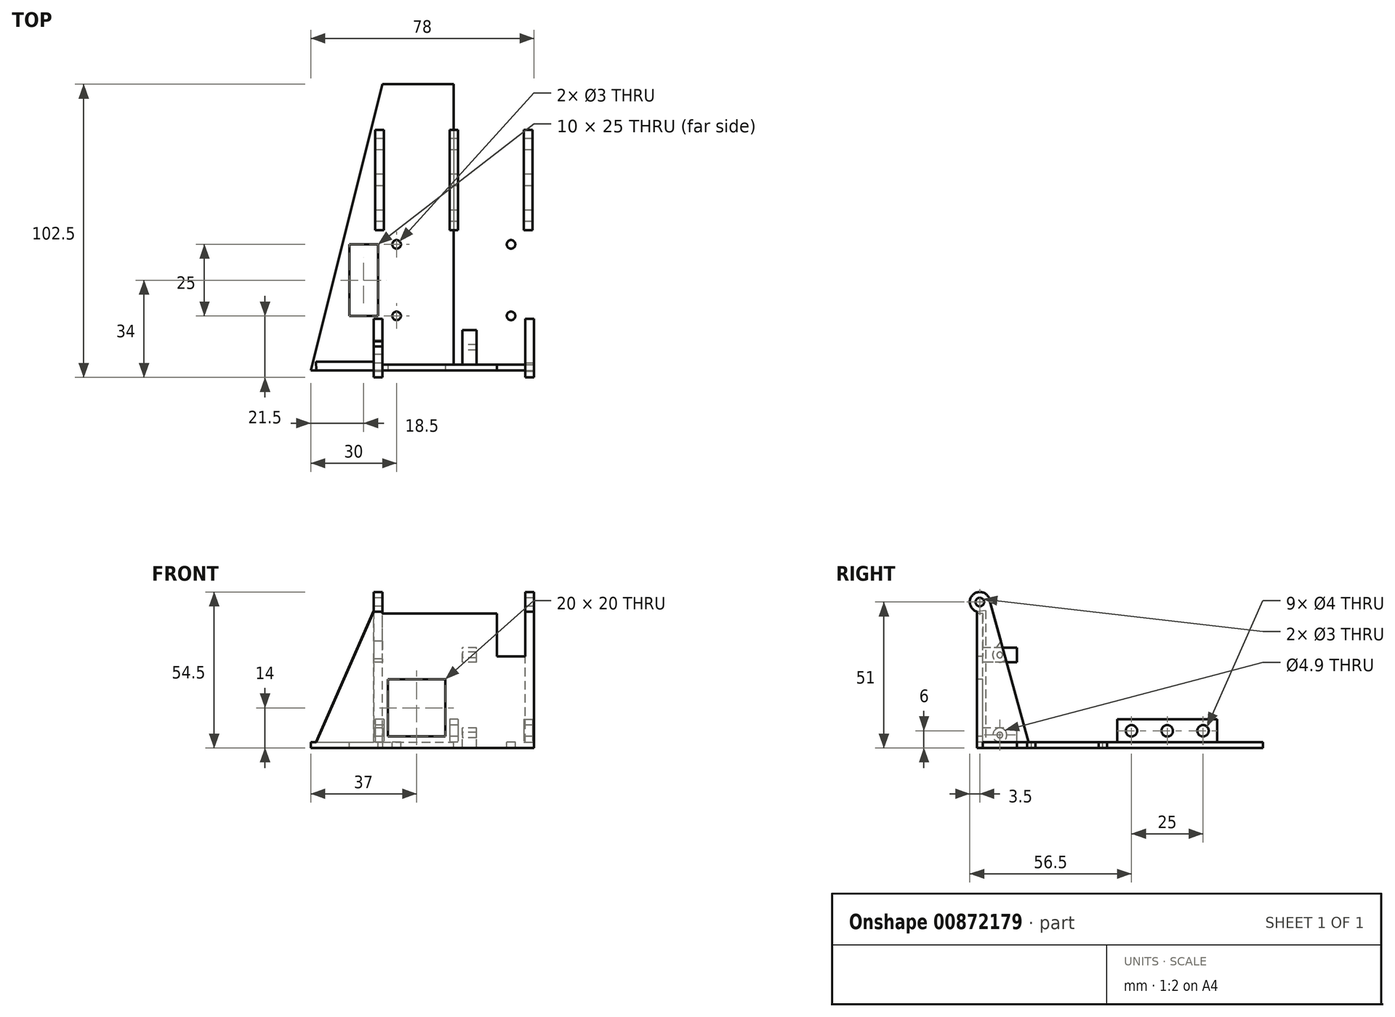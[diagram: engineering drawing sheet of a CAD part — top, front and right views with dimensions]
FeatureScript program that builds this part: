
annotation { "Feature Type Name" : "Feature", "Feature Type Description" : "" }
export const myFeature = defineFeature(function(context is Context, id is Id, definition is map)
    precondition{}
    {
        {
            var Q0;
            Q0=qCreatedBy(makeId("Top.planeOp"),FACE);
            var sketch = newSketch(context, id + "F0", { "sketchPlane" : qUnion([Q0])});
            skLineSegment(sketch, "E0.bottom", {"start": v(25, -50) * mm, "end": v(-25, -50) * mm});
            skLineSegment(sketch, "E0.top", {"start": v(25, 50) * mm, "end": v(-25, 50) * mm});
            skLineSegment(sketch, "E0.left", {"start": v(25, -50) * mm, "end": v(25, 50) * mm});
            skLineSegment(sketch, "E0.right", {"start": v(-25, -50) * mm, "end": v(-25, 50) * mm});
            skPoint(sketch, "E0.middle", {"position": v(0, 0) * mm});
            skLineSegment(sketch, "E1", {"start": v(-25, -50) * mm, "end": v(-50, -50) * mm});
            skLineSegment(sketch, "E2", {"start": v(-50, -50) * mm, "end": v(-25, 50) * mm});
            skLineSegment(sketch, "E3", {"start": v(25, -50) * mm, "end": v(50, -50) * mm});
            skLineSegment(sketch, "E4", {"start": v(50, -50) * mm, "end": v(25, 50) * mm});
            skSolve(sketch);
        }
        {
            var Q0;
            Q0=makeQuery(id+"F0.imprint","IMPRINT",FACE,{"disambiguationData":[TD([[makeQuery(id+"F0.imprint","IMPRINT",EDGE,{"derivedFrom":sQuery(id+"F0.wireOp",EDGE,"E0.left")}),-1.0]])]});
            var Q1;
            Q1=makeQuery(id+"F0.imprint","IMPRINT",FACE,{"disambiguationData":[TD([[makeQuery(id+"F0.imprint","IMPRINT",EDGE,{"derivedFrom":sQuery(id+"F0.wireOp",EDGE,"E0.right")}),1.0]])]});
            var Q2;
            Q2=makeQuery(id+"F0.imprint","IMPRINT",FACE,{"disambiguationData":[TD([[makeQuery(id+"F0.imprint","IMPRINT",EDGE,{"derivedFrom":sQuery(id+"F0.wireOp",EDGE,"E0.bottom")}),-1.0]])]});
            extrude(context, id + "F1", {"entities" : qUnion([Q0, Q1, Q2]), "depth" : 2 * mm, "offsetDistance" : 25 * mm});
        }
        {
            var Q0;
            Q0=qCreatedBy(makeId("Right.planeOp"),FACE);
            var sketch = newSketch(context, id + "F2", { "sketchPlane" : qUnion([Q0])});
            skLineSegment(sketch, "E5.bottom", {"start": v(-50, 0) * mm, "end": v(-48, 0) * mm});
            skLineSegment(sketch, "E5.top", {"start": v(-50, 47) * mm, "end": v(-48, 47) * mm});
            skLineSegment(sketch, "E5.left", {"start": v(-50, 0) * mm, "end": v(-50, 47) * mm});
            skLineSegment(sketch, "E5.right", {"start": v(-48, 0) * mm, "end": v(-48, 47) * mm});
            skSolve(sketch);
        }
        {
            var Q0;
            Q0=makeQuery(id+"F2.imprint","IMPRINT",FACE,{"disambiguationData":[TD([[makeQuery(id+"F2.imprint","IMPRINT",EDGE,{"derivedFrom":sQuery(id+"F2.wireOp",EDGE,"E5.bottom")}),1.0]])]});
            extrude(context, id + "F3", {"entities" : qUnion([Q0]), "operationType" : NewBodyOperationType.ADD, "endBound" : BoundingType.SYMMETRIC, "depth" : 56 * mm, "offsetDistance" : 25 * mm});
        }
        {
            var Q0;
            Q0=makeQuery(id+"F3.opExtrude","CAP_FACE",FACE,{"disambiguationData":[OSD([sQuery(id+"F2.wireOp",EDGE,"E5.bottom"),sQuery(id+"F2.wireOp",EDGE,"E5.top"),sQuery(id+"F2.wireOp",EDGE,"E5.left"),sQuery(id+"F2.wireOp",EDGE,"E5.right")])],"isStart":false});
            var sketch = newSketch(context, id + "F4", { "sketchPlane" : qUnion([Q0])});
            skPoint(sketch, "E6.centerSnap0", {"position": v(-49, 47) * mm});
            skCircle(sketch, "E7", {"center": v(-49, 51) * mm, "radius": 3.5 * mm});
            skLineSegment(sketch, "E8", {"start": v(-48, 47) * mm, "end": v(-48, 47.65) * mm});
            skLineSegment(sketch, "E9", {"start": v(-50, 47) * mm, "end": v(-50, 47.65) * mm});
            skSolve(sketch);
        }
        {
            var Q0;
            {var subQ5=makeQuery(id+"F3.opExtrude","CAP_EDGE",EDGE,{"disambiguationData":[OSD([sQuery(id+"F2.wireOp",EDGE,"E5.top")])],"isStart":false});Q0=makeQuery(id+"F4.imprint","IMPRINT",FACE,{"disambiguationData":[TD([[makeQuery(id+"F4.imprint","IMPRINT",EDGE,{"derivedFrom":subQ5}),1.0]])]});}
            var Q1;
            {var subQ0=sQuery(id+"F4.wireOp",EDGE,"E7");var subQ1=makeQuery(id+"F4.imprint","INTERSECT",VERTEX,{"derivedFrom":[subQ0,sQuery(id+"F4.wireOp",EDGE,"E8")]});Q1=makeQuery(id+"F4.imprint","IMPRINT",FACE,{"disambiguationData":[TD([[makeQuery(id+"F4.imprint","IMPRINT",EDGE,{"disambiguationData":[TD([[subQ1,1.0]])],"derivedFrom":subQ0}),1.0]])]});}
            extrude(context, id + "F5", {"entities" : qUnion([Q0, Q1]), "operationType" : NewBodyOperationType.ADD, "oppositeDirection" : true, "depth" : 3 * mm, "offsetDistance" : 25 * mm});
        }
        {
            var Q0;
            Q0=makeQuery(id+"F3.opExtrude","CAP_FACE",FACE,{"disambiguationData":[OSD([sQuery(id+"F2.wireOp",EDGE,"E5.bottom"),sQuery(id+"F2.wireOp",EDGE,"E5.top"),sQuery(id+"F2.wireOp",EDGE,"E5.left"),sQuery(id+"F2.wireOp",EDGE,"E5.right")])],"isStart":true});
            var sketch = newSketch(context, id + "F6", { "sketchPlane" : qUnion([Q0])});
            skCircle(sketch, "E10", {"center": v(49, 51) * mm, "radius": 3.5 * mm});
            skPoint(sketch, "E10.centerSnap0", {"position": v(49, 47) * mm});
            skLineSegment(sketch, "E11", {"start": v(48, 47) * mm, "end": v(48, 47.65) * mm});
            skLineSegment(sketch, "E12", {"start": v(50, 47) * mm, "end": v(50, 47.65) * mm});
            skSolve(sketch);
        }
        {
            var Q0;
            {var subQ5=makeQuery(id+"F3.opExtrude","CAP_EDGE",EDGE,{"disambiguationData":[OSD([sQuery(id+"F2.wireOp",EDGE,"E5.top")])],"isStart":true});Q0=makeQuery(id+"F6.imprint","IMPRINT",FACE,{"disambiguationData":[TD([[makeQuery(id+"F6.imprint","IMPRINT",EDGE,{"derivedFrom":subQ5}),-1.0]])]});}
            var Q1;
            {var subQ0=sQuery(id+"F6.wireOp",EDGE,"E10");var subQ1=makeQuery(id+"F6.imprint","INTERSECT",VERTEX,{"derivedFrom":[subQ0,sQuery(id+"F6.wireOp",EDGE,"E11")]});Q1=makeQuery(id+"F6.imprint","IMPRINT",FACE,{"disambiguationData":[TD([[makeQuery(id+"F6.imprint","IMPRINT",EDGE,{"disambiguationData":[TD([[subQ1,-1.0]])],"derivedFrom":subQ0}),1.0]])]});}
            extrude(context, id + "F7", {"entities" : qUnion([Q0, Q1]), "operationType" : NewBodyOperationType.ADD, "oppositeDirection" : true, "depth" : 3 * mm, "offsetDistance" : 25 * mm});
        }
        {
            var Q0;
            {var subQ0=sQuery(id+"F2.wireOp",EDGE,"E5.right");var subQ1=sQuery(id+"F2.wireOp",EDGE,"E5.left");var subQ2=sQuery(id+"F2.wireOp",EDGE,"E5.top");Q0=makeQuery(id+"F7.boolean.opBoolean","MERGE",FACE,{"derivedFrom":[makeQuery(id+"F3.opExtrude","CAP_FACE",FACE,{"disambiguationData":[OSD([sQuery(id+"F2.wireOp",EDGE,"E5.bottom"),subQ2,subQ1,subQ0])],"isStart":true}),makeQuery(id+"F7.opExtrude","CAP_FACE",FACE,{"disambiguationData":[OSD([subQ2,subQ1,subQ0,sQuery(id+"F6.wireOp",EDGE,"E10")])],"isStart":true})]});}
            var sketch = newSketch(context, id + "F8", { "sketchPlane" : qUnion([Q0])});
            skCircle(sketch, "E13", {"center": v(49, 51) * mm, "radius": 1.5 * mm});
            skSolve(sketch);
        }
        {
            var Q0;
            Q0=makeQuery(id+"F8.imprint","IMPRINT",FACE,{"disambiguationData":[TD([[makeQuery(id+"F8.imprint","IMPRINT",EDGE,{"derivedFrom":sQuery(id+"F8.wireOp",EDGE,"E13")}),1.0]])]});
            extrude(context, id + "F9", {"entities" : qUnion([Q0]), "operationType" : NewBodyOperationType.REMOVE, "oppositeDirection" : true, "depth" : 60 * mm, "offsetDistance" : 25 * mm});
        }
        {
            var Q0;
            Q0=makeQuery(id+"F7.boolean.opBoolean","MERGE",FACE,{"derivedFrom":[makeQuery(id+"F5.boolean.opBoolean","MERGE",FACE,{"derivedFrom":[makeQuery(id+"F3.opExtrude","SWEPT_FACE",FACE,{"disambiguationData":[OSD([sQuery(id+"F2.wireOp",EDGE,"E5.right")])]}),makeQuery(id+"F5.opExtrude","SWEPT_FACE",FACE,{"disambiguationData":[OSD([sQuery(id+"F4.wireOp",EDGE,"E8")])]})]}),makeQuery(id+"F7.opExtrude","SWEPT_FACE",FACE,{"disambiguationData":[OSD([sQuery(id+"F6.wireOp",EDGE,"E11")])]})]});
            var sketch = newSketch(context, id + "F10", { "sketchPlane" : qUnion([Q0])});
            skLineSegment(sketch, "E14.bottom", {"start": v(-8, 2) * mm, "end": v(-3, 2) * mm});
            skLineSegment(sketch, "E14.top", {"start": v(-8, 7) * mm, "end": v(-3, 7) * mm});
            skLineSegment(sketch, "E14.left", {"start": v(-3, 2) * mm, "end": v(-3, 7) * mm});
            skLineSegment(sketch, "E14.right", {"start": v(-8, 2) * mm, "end": v(-8, 7) * mm});
            skLineSegment(sketch, "E15.bottom", {"start": v(-8, 30) * mm, "end": v(-3, 30) * mm});
            skLineSegment(sketch, "E15.top", {"start": v(-8, 35) * mm, "end": v(-3, 35) * mm});
            skLineSegment(sketch, "E15.left", {"start": v(-3, 30) * mm, "end": v(-3, 35) * mm});
            skLineSegment(sketch, "E15.right", {"start": v(-8, 30) * mm, "end": v(-8, 35) * mm});
            skSolve(sketch);
        }
        {
            var Q0;
            Q0=makeQuery(id+"F10.imprint","IMPRINT",FACE,{"disambiguationData":[TD([[makeQuery(id+"F10.imprint","IMPRINT",EDGE,{"derivedFrom":sQuery(id+"F10.wireOp",EDGE,"E15.bottom")}),1.0]])]});
            var Q1;
            Q1=makeQuery(id+"F10.imprint","IMPRINT",FACE,{"disambiguationData":[TD([[makeQuery(id+"F10.imprint","IMPRINT",EDGE,{"derivedFrom":sQuery(id+"F10.wireOp",EDGE,"E14.bottom")}),-1.0]])]});
            extrude(context, id + "F11", {"entities" : qUnion([Q0, Q1]), "operationType" : NewBodyOperationType.ADD, "depth" : 12 * mm, "offsetDistance" : 25 * mm});
        }
        {
            var Q0;
            Q0=makeQuery(id+"F11.opExtrude","SWEPT_FACE",FACE,{"disambiguationData":[OSD([sQuery(id+"F10.wireOp",EDGE,"E14.left")])]});
            var sketch = newSketch(context, id + "F12", { "sketchPlane" : qUnion([Q0])});
            skCircle(sketch, "E16", {"center": v(42, 4.5) * mm, "radius": 1 * mm});
            skPoint(sketch, "E16.centerSnap0", {"position": v(36, 4.5) * mm});
            skPoint(sketch, "E16.centerSnap1", {"position": v(42, 7) * mm});
            skSolve(sketch);
        }
        {
            var Q0;
            Q0=makeQuery(id+"F12.imprint","IMPRINT",FACE,{"disambiguationData":[TD([[makeQuery(id+"F12.imprint","IMPRINT",EDGE,{"derivedFrom":sQuery(id+"F12.wireOp",EDGE,"E16")}),1.0]])]});
            extrude(context, id + "F13", {"entities" : qUnion([Q0]), "operationType" : NewBodyOperationType.REMOVE, "oppositeDirection" : true, "depth" : 25 * mm, "offsetDistance" : 25 * mm});
        }
        {
            var Q0;
            Q0=makeQuery(id+"F11.opExtrude","SWEPT_FACE",FACE,{"disambiguationData":[OSD([sQuery(id+"F10.wireOp",EDGE,"E15.left")])]});
            var sketch = newSketch(context, id + "F14", { "sketchPlane" : qUnion([Q0])});
            skCircle(sketch, "E17", {"center": v(42, 32.5) * mm, "radius": 1 * mm});
            skPoint(sketch, "E17.centerSnap0", {"position": v(42, 35) * mm});
            skPoint(sketch, "E17.centerSnap1", {"position": v(36, 32.5) * mm});
            skSolve(sketch);
        }
        {
            var Q0;
            Q0=makeQuery(id+"F14.imprint","IMPRINT",FACE,{"disambiguationData":[TD([[makeQuery(id+"F14.imprint","IMPRINT",EDGE,{"derivedFrom":sQuery(id+"F14.wireOp",EDGE,"E17")}),1.0]])]});
            extrude(context, id + "F15", {"entities" : qUnion([Q0]), "operationType" : NewBodyOperationType.REMOVE, "oppositeDirection" : true, "depth" : 25 * mm, "offsetDistance" : 25 * mm});
        }
        {
            var Q0;
            Q0=makeQuery(id+"F7.boolean.opBoolean","MERGE",FACE,{"derivedFrom":[makeQuery(id+"F5.boolean.opBoolean","MERGE",FACE,{"derivedFrom":[makeQuery(id+"F3.boolean.opBoolean","MERGE",FACE,{"derivedFrom":[makeQuery(id+"F1.opExtrude","SWEPT_FACE",FACE,{"disambiguationData":[OSD([sQuery(id+"F0.wireOp",EDGE,"E0.bottom"),sQuery(id+"F0.wireOp",EDGE,"E1"),sQuery(id+"F0.wireOp",EDGE,"E3")])]}),makeQuery(id+"F3.opExtrude","SWEPT_FACE",FACE,{"disambiguationData":[OSD([sQuery(id+"F2.wireOp",EDGE,"E5.left")])]})]}),makeQuery(id+"F5.opExtrude","SWEPT_FACE",FACE,{"disambiguationData":[OSD([sQuery(id+"F4.wireOp",EDGE,"E9")])]})]}),makeQuery(id+"F7.opExtrude","SWEPT_FACE",FACE,{"disambiguationData":[OSD([sQuery(id+"F6.wireOp",EDGE,"E12")])]})]});
            var sketch = newSketch(context, id + "F16", { "sketchPlane" : qUnion([Q0])});
            skLineSegment(sketch, "E18.bottom", {"start": v(-23, 4) * mm, "end": v(-3, 4) * mm});
            skLineSegment(sketch, "E18.top", {"start": v(-23, 24) * mm, "end": v(-3, 24) * mm});
            skLineSegment(sketch, "E18.left", {"start": v(-23, 4) * mm, "end": v(-23, 24) * mm});
            skLineSegment(sketch, "E18.right", {"start": v(-3, 4) * mm, "end": v(-3, 24) * mm});
            skLineSegment(sketch, "E19.bottom", {"start": v(25, 47) * mm, "end": v(15, 47) * mm});
            skLineSegment(sketch, "E19.top", {"start": v(25, 32) * mm, "end": v(15, 32) * mm});
            skLineSegment(sketch, "E19.left", {"start": v(25, 47) * mm, "end": v(25, 32) * mm});
            skLineSegment(sketch, "E19.right", {"start": v(15, 47) * mm, "end": v(15, 32) * mm});
            skSolve(sketch);
        }
        {
            var Q0;
            Q0=makeQuery(id+"F16.imprint","IMPRINT",FACE,{"disambiguationData":[TD([[makeQuery(id+"F16.imprint","IMPRINT",EDGE,{"derivedFrom":sQuery(id+"F16.wireOp",EDGE,"E19.bottom")}),1.0]])]});
            var Q1;
            Q1=makeQuery(id+"F16.imprint","IMPRINT",FACE,{"disambiguationData":[TD([[makeQuery(id+"F16.imprint","IMPRINT",EDGE,{"derivedFrom":sQuery(id+"F16.wireOp",EDGE,"E18.bottom")}),1.0]])]});
            extrude(context, id + "F17", {"entities" : qUnion([Q0, Q1]), "operationType" : NewBodyOperationType.REMOVE, "oppositeDirection" : true, "depth" : 25 * mm, "offsetDistance" : 25 * mm});
        }
        {
            var Q0;
            Q0=makeQuery(id+"F1.opExtrude","CAP_FACE",FACE,{"disambiguationData":[OSD([sQuery(id+"F0.wireOp",EDGE,"E0.bottom"),sQuery(id+"F0.wireOp",EDGE,"E0.top"),sQuery(id+"F0.wireOp",EDGE,"E1"),sQuery(id+"F0.wireOp",EDGE,"E2"),sQuery(id+"F0.wireOp",EDGE,"E3"),sQuery(id+"F0.wireOp",EDGE,"E4")])],"isStart":false});
            var sketch = newSketch(context, id + "F18", { "sketchPlane" : qUnion([Q0])});
            skCircle(sketch, "E20", {"center": v(-20, -31) * mm, "radius": 1.5 * mm});
            skCircle(sketch, "E21", {"center": v(-20, -6) * mm, "radius": 1.5 * mm});
            skLineSegment(sketch, "E22", {"start": v(0, 50) * mm, "end": v(0, -48) * mm});
            skCircle(sketch, "E23.MirrorC", {"center": v(20, -31) * mm, "radius": 1.5 * mm});
            skCircle(sketch, "E24.MirrorC", {"center": v(20, -6) * mm, "radius": 1.5 * mm});
            skLineSegment(sketch, "E25.bottom", {"start": v(-36.5, -31) * mm, "end": v(-26.5, -31) * mm});
            skLineSegment(sketch, "E25.top", {"start": v(-36.5, -6) * mm, "end": v(-26.5, -6) * mm});
            skLineSegment(sketch, "E25.left", {"start": v(-36.5, -31) * mm, "end": v(-36.5, -6) * mm});
            skLineSegment(sketch, "E25.right", {"start": v(-26.5, -31) * mm, "end": v(-26.5, -6) * mm});
            skPoint(sketch, "E25.middle", {"position": v(-31.5, -18.5) * mm});
            skLineSegment(sketch, "E26.MirrorCS", {"start": v(36.5, -31) * mm, "end": v(36.5, -6) * mm});
            skLineSegment(sketch, "E27.MirrorCS", {"start": v(36.5, -31) * mm, "end": v(26.5, -31) * mm});
            skLineSegment(sketch, "E28.MirrorCS", {"start": v(26.5, -31) * mm, "end": v(26.5, -6) * mm});
            skLineSegment(sketch, "E29.MirrorCS", {"start": v(36.5, -6) * mm, "end": v(26.5, -6) * mm});
            skSolve(sketch);
        }
        {
            var Q0;
            Q0=makeQuery(id+"F18.imprint","IMPRINT",FACE,{"disambiguationData":[TD([[makeQuery(id+"F18.imprint","IMPRINT",EDGE,{"derivedFrom":sQuery(id+"F18.wireOp",EDGE,"E20")}),1.0]])]});
            var Q1;
            Q1=makeQuery(id+"F18.imprint","IMPRINT",FACE,{"disambiguationData":[TD([[makeQuery(id+"F18.imprint","IMPRINT",EDGE,{"derivedFrom":sQuery(id+"F18.wireOp",EDGE,"E21")}),1.0]])]});
            var Q2;
            Q2=makeQuery(id+"F18.imprint","IMPRINT",FACE,{"disambiguationData":[TD([[makeQuery(id+"F18.imprint","IMPRINT",EDGE,{"derivedFrom":sQuery(id+"F18.wireOp",EDGE,"E23.MirrorC")}),-1.0]])]});
            var Q3;
            Q3=makeQuery(id+"F18.imprint","IMPRINT",FACE,{"disambiguationData":[TD([[makeQuery(id+"F18.imprint","IMPRINT",EDGE,{"derivedFrom":sQuery(id+"F18.wireOp",EDGE,"E24.MirrorC")}),-1.0]])]});
            var Q4;
            Q4=makeQuery(id+"F18.imprint","IMPRINT",FACE,{"disambiguationData":[TD([[makeQuery(id+"F18.imprint","IMPRINT",EDGE,{"derivedFrom":sQuery(id+"F18.wireOp",EDGE,"E25.bottom")}),1.0]])]});
            var Q5;
            Q5=makeQuery(id+"F18.imprint","IMPRINT",FACE,{"disambiguationData":[TD([[makeQuery(id+"F18.imprint","IMPRINT",EDGE,{"derivedFrom":sQuery(id+"F18.wireOp",EDGE,"E26.MirrorCS")}),1.0]])]});
            extrude(context, id + "F19", {"entities" : qUnion([Q0, Q1, Q2, Q3, Q4, Q5]), "operationType" : NewBodyOperationType.REMOVE, "oppositeDirection" : true, "depth" : 25 * mm, "offsetDistance" : 25 * mm});
        }
        {
            var Q0;
            Q0=makeQuery(id+"F1.opExtrude","CAP_FACE",FACE,{"disambiguationData":[OSD([sQuery(id+"F0.wireOp",EDGE,"E0.bottom"),sQuery(id+"F0.wireOp",EDGE,"E0.top"),sQuery(id+"F0.wireOp",EDGE,"E1"),sQuery(id+"F0.wireOp",EDGE,"E2"),sQuery(id+"F0.wireOp",EDGE,"E3"),sQuery(id+"F0.wireOp",EDGE,"E4")])],"isStart":false});
            var sketch = newSketch(context, id + "F20", { "sketchPlane" : qUnion([Q0])});
            skLineSegment(sketch, "E30.bottom", {"start": v(1.5, -1) * mm, "end": v(-1.5, -1) * mm});
            skLineSegment(sketch, "E30.top", {"start": v(1.5, 34) * mm, "end": v(-1.5, 34) * mm});
            skLineSegment(sketch, "E30.left", {"start": v(1.5, -1) * mm, "end": v(1.5, 34) * mm});
            skLineSegment(sketch, "E30.right", {"start": v(-1.5, -1) * mm, "end": v(-1.5, 34) * mm});
            skPoint(sketch, "E30.middle", {"position": v(0, 16.5) * mm});
            skLineSegment(sketch, "E31.bottom", {"start": v(-24.5, -1) * mm, "end": v(-27.5, -1) * mm});
            skLineSegment(sketch, "E31.top", {"start": v(-24.5, 34) * mm, "end": v(-27.5, 34) * mm});
            skLineSegment(sketch, "E31.left", {"start": v(-24.5, -1) * mm, "end": v(-24.5, 34) * mm});
            skLineSegment(sketch, "E31.right", {"start": v(-27.5, -1) * mm, "end": v(-27.5, 34) * mm});
            skLineSegment(sketch, "E32.bottom", {"start": v(24.5, -1) * mm, "end": v(27.5, -1) * mm});
            skLineSegment(sketch, "E32.top", {"start": v(24.5, 34) * mm, "end": v(27.5, 34) * mm});
            skLineSegment(sketch, "E32.left", {"start": v(24.5, -1) * mm, "end": v(24.5, 34) * mm});
            skLineSegment(sketch, "E32.right", {"start": v(27.5, -1) * mm, "end": v(27.5, 34) * mm});
            skSolve(sketch);
        }
        {
            var Q0;
            Q0=makeQuery(id+"F20.imprint","IMPRINT",FACE,{"disambiguationData":[TD([[makeQuery(id+"F20.imprint","IMPRINT",EDGE,{"derivedFrom":sQuery(id+"F20.wireOp",EDGE,"E31.bottom")}),-1.0]])]});
            var Q1;
            Q1=makeQuery(id+"F20.imprint","IMPRINT",FACE,{"disambiguationData":[TD([[makeQuery(id+"F20.imprint","IMPRINT",EDGE,{"derivedFrom":sQuery(id+"F20.wireOp",EDGE,"E30.bottom")}),-1.0]])]});
            var Q2;
            Q2=makeQuery(id+"F20.imprint","IMPRINT",FACE,{"disambiguationData":[TD([[makeQuery(id+"F20.imprint","IMPRINT",EDGE,{"derivedFrom":sQuery(id+"F20.wireOp",EDGE,"E32.bottom")}),1.0]])]});
            extrude(context, id + "F21", {"entities" : qUnion([Q0, Q1, Q2]), "operationType" : NewBodyOperationType.ADD, "depth" : 8 * mm, "offsetDistance" : 25 * mm});
        }
        {
            var Q0;
            Q0=makeQuery(id+"F21.opExtrude","SWEPT_FACE",FACE,{"disambiguationData":[OSD([sQuery(id+"F20.wireOp",EDGE,"E31.right")])]});
            var sketch = newSketch(context, id + "F22", { "sketchPlane" : qUnion([Q0])});
            skCircle(sketch, "E33", {"center": v(-4, 6) * mm, "radius": 2 * mm});
            skPoint(sketch, "E33.centerSnap0", {"position": v(1, 6) * mm});
            skCircle(sketch, "E34", {"center": v(-29, 6) * mm, "radius": 2 * mm});
            skPoint(sketch, "E34.centerSnap0", {"position": v(-34, 6) * mm});
            skCircle(sketch, "E35", {"center": v(-16.5, 6) * mm, "radius": 2 * mm});
            skPoint(sketch, "E35.centerSnap0", {"position": v(-16.5, 10) * mm});
            skSolve(sketch);
        }
        {
            var Q0;
            Q0=makeQuery(id+"F22.imprint","IMPRINT",FACE,{"disambiguationData":[TD([[makeQuery(id+"F22.imprint","IMPRINT",EDGE,{"derivedFrom":sQuery(id+"F22.wireOp",EDGE,"E34")}),1.0]])]});
            var Q1;
            Q1=makeQuery(id+"F22.imprint","IMPRINT",FACE,{"disambiguationData":[TD([[makeQuery(id+"F22.imprint","IMPRINT",EDGE,{"derivedFrom":sQuery(id+"F22.wireOp",EDGE,"E35")}),1.0]])]});
            var Q2;
            Q2=makeQuery(id+"F22.imprint","IMPRINT",FACE,{"disambiguationData":[TD([[makeQuery(id+"F22.imprint","IMPRINT",EDGE,{"derivedFrom":sQuery(id+"F22.wireOp",EDGE,"E33")}),1.0]])]});
            extrude(context, id + "F23", {"entities" : qUnion([Q0, Q1, Q2]), "operationType" : NewBodyOperationType.REMOVE, "oppositeDirection" : true, "depth" : 100 * mm, "offsetDistance" : 25 * mm});
        }
        {
            var Q0;
            Q0=makeQuery(id+"F7.boolean.opBoolean","MERGE",FACE,{"derivedFrom":[makeQuery(id+"F5.boolean.opBoolean","MERGE",FACE,{"derivedFrom":[makeQuery(id+"F3.boolean.opBoolean","MERGE",FACE,{"derivedFrom":[makeQuery(id+"F1.opExtrude","SWEPT_FACE",FACE,{"disambiguationData":[OSD([sQuery(id+"F0.wireOp",EDGE,"E0.bottom"),sQuery(id+"F0.wireOp",EDGE,"E1"),sQuery(id+"F0.wireOp",EDGE,"E3")])]}),makeQuery(id+"F3.opExtrude","SWEPT_FACE",FACE,{"disambiguationData":[OSD([sQuery(id+"F2.wireOp",EDGE,"E5.left")])]})]}),makeQuery(id+"F5.opExtrude","SWEPT_FACE",FACE,{"disambiguationData":[OSD([sQuery(id+"F4.wireOp",EDGE,"E9")])]})]}),makeQuery(id+"F7.opExtrude","SWEPT_FACE",FACE,{"disambiguationData":[OSD([sQuery(id+"F6.wireOp",EDGE,"E12")])]})]});
            var sketch = newSketch(context, id + "F24", { "sketchPlane" : qUnion([Q0])});
            skLineSegment(sketch, "E36", {"start": v(28, 47.65) * mm, "end": v(48, 2) * mm});
            skLineSegment(sketch, "E37", {"start": v(-28, 47.65) * mm, "end": v(-48, 2) * mm});
            skSolve(sketch);
        }
        {
            var Q0;
            {var subQ0=sQuery(id+"F24.wireOp",EDGE,"E36");Q0=makeQuery(id+"F24.imprint","IMPRINT",FACE,{"disambiguationData":[TD([[makeQuery(id+"F24.imprint","IMPRINT",EDGE,{"derivedFrom":subQ0}),-1.0]])]});}
            var Q1;
            {var subQ0=sQuery(id+"F24.wireOp",EDGE,"E37");Q1=makeQuery(id+"F24.imprint","IMPRINT",FACE,{"disambiguationData":[TD([[makeQuery(id+"F24.imprint","IMPRINT",EDGE,{"derivedFrom":subQ0}),1.0]])]});}
            extrude(context, id + "F25", {"entities" : qUnion([Q0, Q1]), "oppositeDirection" : true, "depth" : 3 * mm, "offsetDistance" : 25 * mm, "hasDraft" : true, "draftAngle" : 3 * degree});
        }
        {
            var Q0;
            {var subQ0=sQuery(id+"F2.wireOp",EDGE,"E5.top");Q0=makeQuery(id+"F5.boolean.opBoolean","MERGE",FACE,{"derivedFrom":[makeQuery(id+"F3.opExtrude","CAP_FACE",FACE,{"disambiguationData":[OSD([sQuery(id+"F2.wireOp",EDGE,"E5.bottom"),subQ0,sQuery(id+"F2.wireOp",EDGE,"E5.left"),sQuery(id+"F2.wireOp",EDGE,"E5.right")])],"isStart":false}),makeQuery(id+"F5.opExtrude","CAP_FACE",FACE,{"disambiguationData":[OSD([subQ0,sQuery(id+"F4.wireOp",EDGE,"E7"),sQuery(id+"F4.wireOp",EDGE,"E8"),sQuery(id+"F4.wireOp",EDGE,"E9")])],"isStart":true})]});}
            var sketch = newSketch(context, id + "F26", { "sketchPlane" : qUnion([Q0])});
            skLineSegment(sketch, "E38", {"start": v(-32, 2) * mm, "end": v(-45.62, 51.92) * mm});
            skLineSegment(sketch, "E39", {"start": v(-32, 2) * mm, "end": v(-48, 2) * mm});
            skLineSegment(sketch, "E40", {"start": v(-48, 2) * mm, "end": v(-48, 47.65) * mm});
            skArc(sketch, "E41", {"start": v(-48, 47.65) * mm, "mid": v(-45.94, 49.3) * mm, "end": v(-45.62, 51.92) * mm});
            skSolve(sketch);
        }
        {
            var Q0;
            Q0=makeQuery(id+"F26.imprint","IMPRINT",FACE,{"disambiguationData":[TD([[makeQuery(id+"F26.imprint","IMPRINT",EDGE,{"derivedFrom":sQuery(id+"F26.wireOp",EDGE,"E38")}),1.0]])]});
            extrude(context, id + "F27", {"entities" : qUnion([Q0]), "operationType" : NewBodyOperationType.ADD, "oppositeDirection" : true, "depth" : 3 * mm, "offsetDistance" : 25 * mm});
        }
        {
            var Q0;
            {var subQ0=sQuery(id+"F2.wireOp",EDGE,"E5.top");Q0=makeQuery(id+"F7.boolean.opBoolean","MERGE",FACE,{"derivedFrom":[makeQuery(id+"F3.opExtrude","CAP_FACE",FACE,{"disambiguationData":[OSD([sQuery(id+"F2.wireOp",EDGE,"E5.bottom"),subQ0,sQuery(id+"F2.wireOp",EDGE,"E5.left"),sQuery(id+"F2.wireOp",EDGE,"E5.right")])],"isStart":true}),makeQuery(id+"F7.opExtrude","CAP_FACE",FACE,{"disambiguationData":[OSD([subQ0,sQuery(id+"F6.wireOp",EDGE,"E10"),sQuery(id+"F6.wireOp",EDGE,"E11"),sQuery(id+"F6.wireOp",EDGE,"E12")])],"isStart":true})]});}
            var sketch = newSketch(context, id + "F28", { "sketchPlane" : qUnion([Q0])});
            skLineSegment(sketch, "E42", {"start": v(32, 2) * mm, "end": v(45.62, 51.92) * mm});
            skLineSegment(sketch, "E43", {"start": v(32, 2) * mm, "end": v(48, 2) * mm});
            skLineSegment(sketch, "E44", {"start": v(48, 2) * mm, "end": v(48, 47.65) * mm});
            skArc(sketch, "E45", {"start": v(48, 47.65) * mm, "mid": v(45.94, 49.3) * mm, "end": v(45.62, 51.92) * mm});
            skCircle(sketch, "E46", {"center": v(42, 32.47) * mm, "radius": 2.5 * mm});
            skLineSegment(sketch, "E47", {"start": v(41.65, 37.37) * mm, "end": v(44.06, 33.9) * mm});
            skCircle(sketch, "E48", {"center": v(42, 4.5) * mm, "radius": 2.45 * mm});
            skSolve(sketch);
        }
        {
            var Q0;
            Q0=makeQuery(id+"F28.imprint","IMPRINT",FACE,{"disambiguationData":[TD([[makeQuery(id+"F28.imprint","IMPRINT",EDGE,{"derivedFrom":sQuery(id+"F28.wireOp",EDGE,"E42")}),-1.0]])]});
            extrude(context, id + "F29", {"entities" : qUnion([Q0]), "operationType" : NewBodyOperationType.ADD, "oppositeDirection" : true, "depth" : 3 * mm, "offsetDistance" : 25 * mm});
        }
    });
